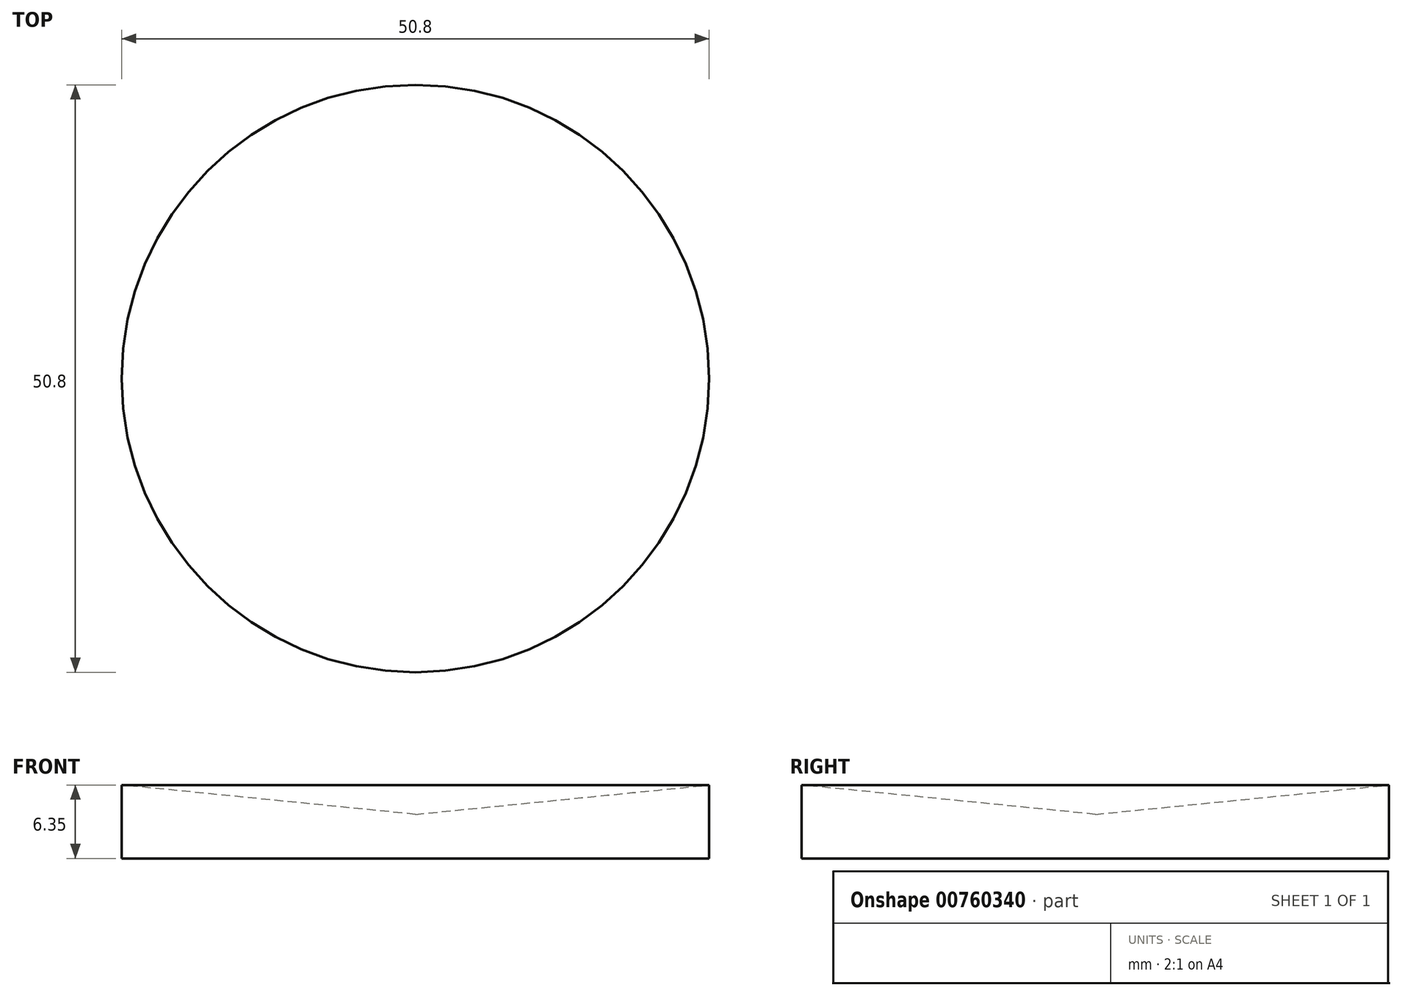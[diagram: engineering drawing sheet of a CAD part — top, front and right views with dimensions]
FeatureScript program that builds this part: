
annotation { "Feature Type Name" : "Feature", "Feature Type Description" : "" }
export const myFeature = defineFeature(function(context is Context, id is Id, definition is map)
    precondition{}
    {
        {
            var Q0;
            Q0=qCreatedBy(makeId("Right.planeOp"),FACE);
            var sketch = newSketch(context, id + "F0", { "sketchPlane" : qUnion([Q0])});
            skLineSegment(sketch, "E0", {"start": v(0, 0) * mm, "end": v(-25.4, 0) * mm});
            skLineSegment(sketch, "E1", {"start": v(-25.4, 0) * mm, "end": v(-25.4, 6.35) * mm});
            skLineSegment(sketch, "E2", {"start": v(-25.4, 6.35) * mm, "end": v(0, 3.8) * mm});
            skLineSegment(sketch, "E3", {"start": v(0, 3.81) * mm, "end": v(0, 0) * mm});
            skSolve(sketch);
        }
        {
            var Q0;
            Q0 = qSketchRegion(id + "F0", true);
            var Q1;
            Q1=sQuery(id+"F0.wireOp",EDGE,"E3");
            revolve(context, id + "F1", {"surfaceOperationType" : NewSurfaceOperationType.NEW, "entities" : qUnion([Q0]), "axis" : qUnion([Q1]), "revolveType" : RevolveType.FULL});
        }
    });
